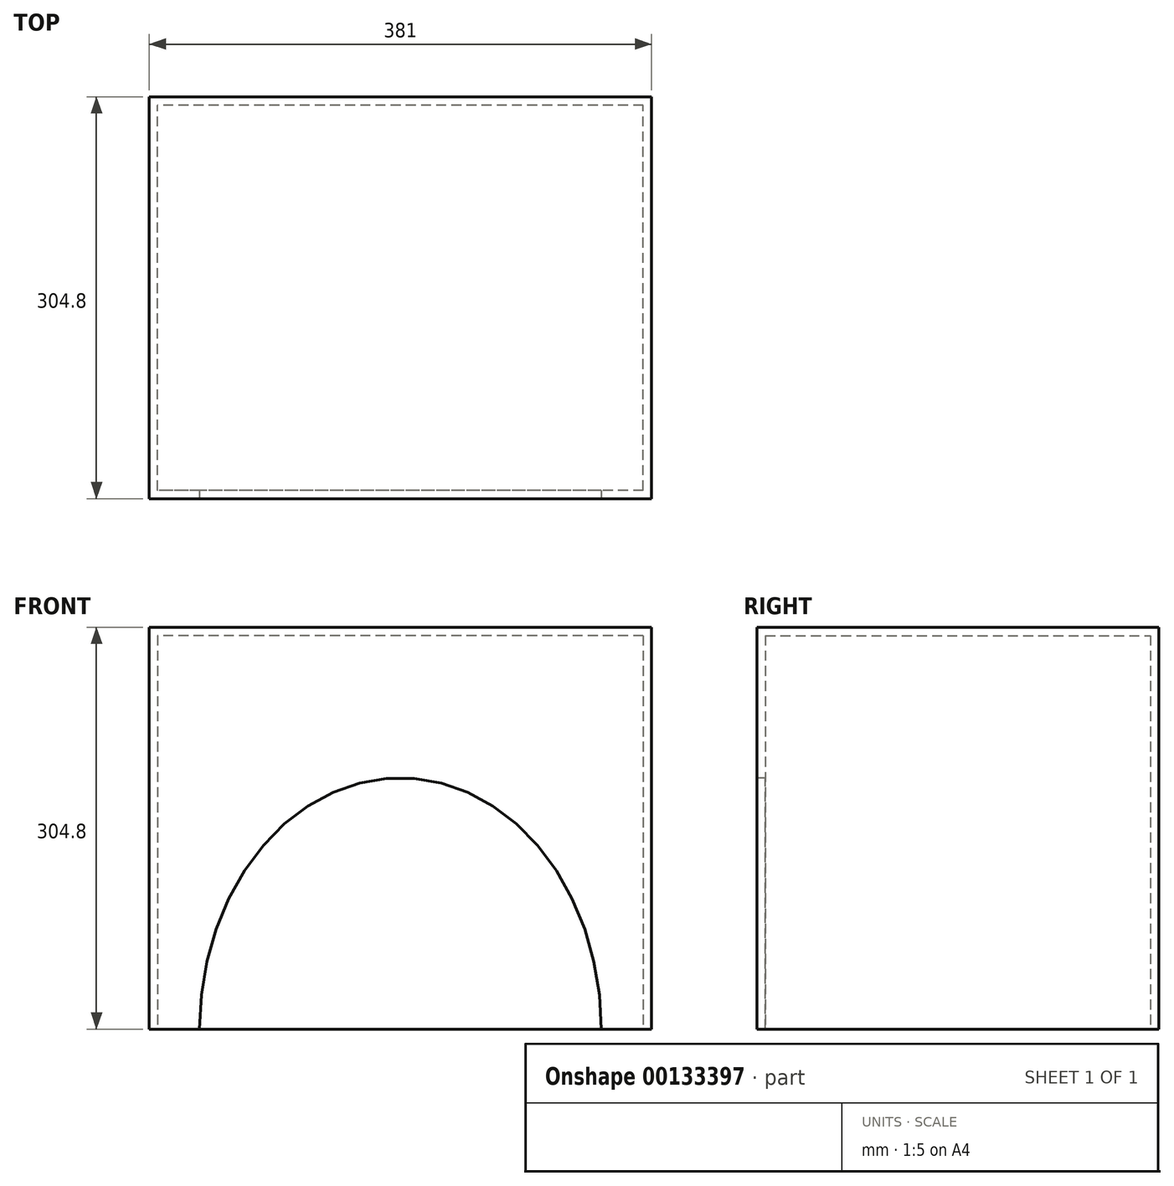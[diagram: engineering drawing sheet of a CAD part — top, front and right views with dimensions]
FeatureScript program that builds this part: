
annotation { "Feature Type Name" : "Feature", "Feature Type Description" : "" }
export const myFeature = defineFeature(function(context is Context, id is Id, definition is map)
    precondition{}
    {
        {
            var Q0;
            Q0=qCreatedBy(makeId("Top.planeOp"),FACE);
            var sketch = newSketch(context, id + "F0", { "sketchPlane" : qUnion([Q0])});
            skLineSegment(sketch, "E0.bottom", {"start": v(190.5, -152.4) * mm, "end": v(-190.5, -152.4) * mm});
            skLineSegment(sketch, "E0.top", {"start": v(190.5, 152.4) * mm, "end": v(-190.5, 152.4) * mm});
            skLineSegment(sketch, "E0.left", {"start": v(190.5, -152.4) * mm, "end": v(190.5, 152.4) * mm});
            skLineSegment(sketch, "E0.right", {"start": v(-190.5, -152.4) * mm, "end": v(-190.5, 152.4) * mm});
            skPoint(sketch, "E0.middle", {"position": v(0, 0) * mm});
            skSolve(sketch);
        }
        {
            var Q0;
            Q0 = qSketchRegion(id + "F0", true);
            extrude(context, id + "F1", {"entities" : qUnion([Q0]), "depth" : 304.8 * mm});
        }
        {
            var Q0;
            Q0=qCreatedBy(makeId("Front.planeOp"),FACE);
            cPlane(context, id + "F2", {"entities" : qUnion([Q0]), "cplaneType" : CPlaneType.OFFSET, "offset" : 254 * mm, "width" : 152.4 * mm, "height" : 152.4 * mm});
        }
        {
            var Q0;
            Q0=qCreatedBy(id+"F2.planeOp",FACE);
            var sketch = newSketch(context, id + "F3", { "sketchPlane" : qUnion([Q0])});
            skEllipse(sketch, "E1", {"center": v(0, 0) * mm, "majorRadius": 190.5 * mm, "minorRadius": 152.4 * mm, "majorAxis": v(0, 1)});
            skPoint(sketch, "E2", {"position": v(0, 190.5) * mm});
            skPoint(sketch, "E3", {"position": v(-152.4, 0) * mm});
            skSolve(sketch);
        }
        {
            var Q0;
            Q0=makeQuery(id+"F1.opExtrude","CAP_FACE",FACE,{"disambiguationData":[OSD([sQuery(id+"F0.wireOp",EDGE,"E0.bottom"),sQuery(id+"F0.wireOp",EDGE,"E0.top"),sQuery(id+"F0.wireOp",EDGE,"E0.left"),sQuery(id+"F0.wireOp",EDGE,"E0.right")])],"isStart":true});
            shell(context, id + "F4", {"entities" : qUnion([Q0]), "thickness" : 6.35 * mm});
        }
        {
            var Q0;
            Q0 = qSketchRegion(id + "F3", true);
            extrude(context, id + "F5", {"entities" : qUnion([Q0]), "operationType" : NewBodyOperationType.REMOVE, "oppositeDirection" : true, "depth" : 127 * mm});
        }
    });
